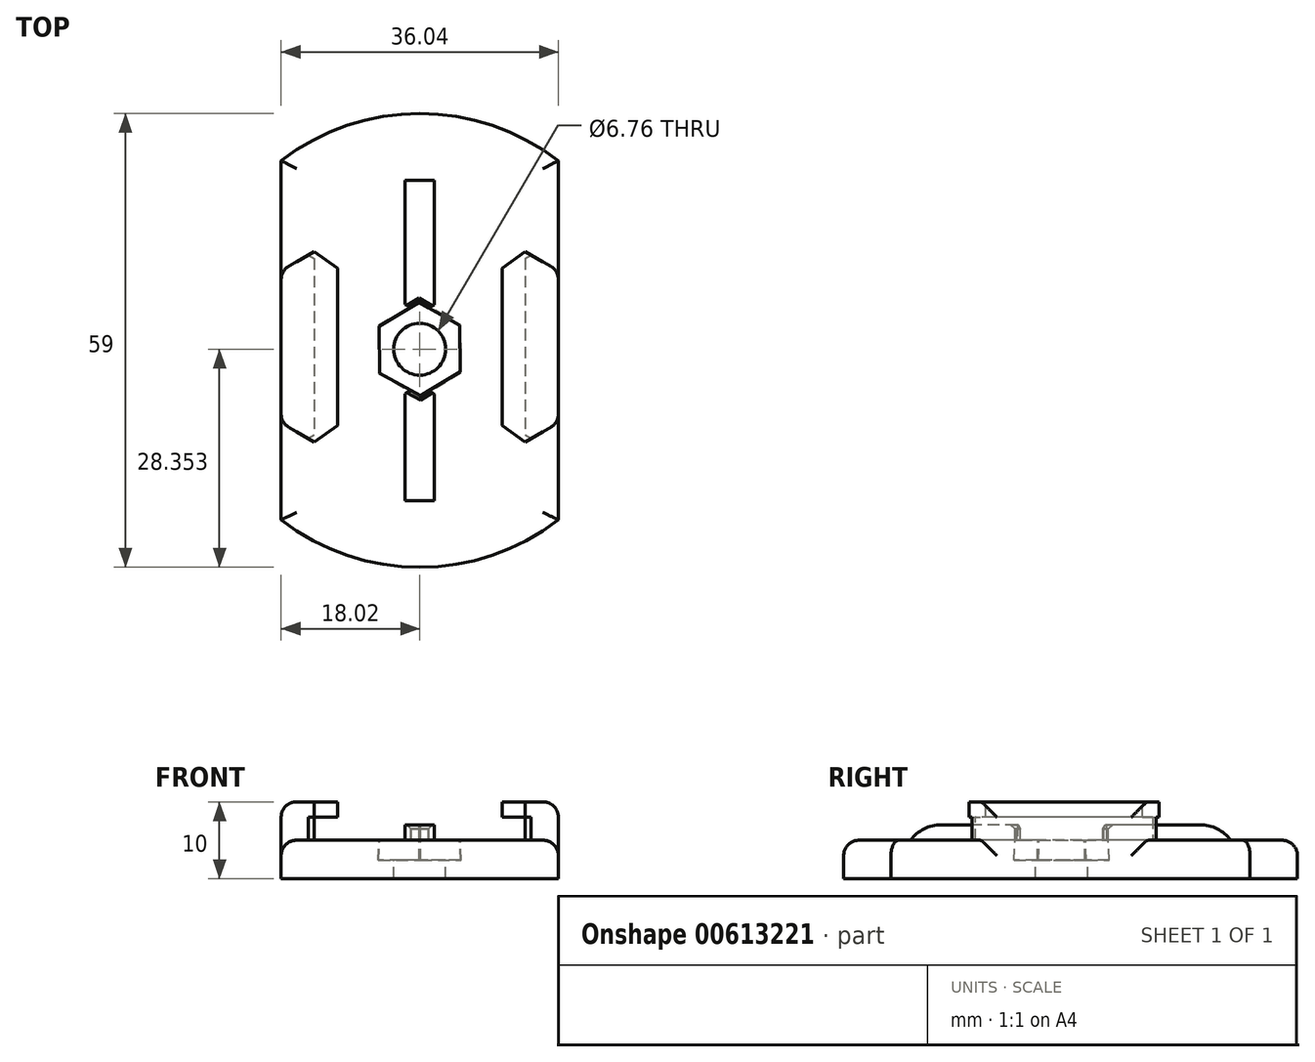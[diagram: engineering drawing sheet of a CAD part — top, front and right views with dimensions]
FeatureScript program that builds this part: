
annotation { "Feature Type Name" : "Feature", "Feature Type Description" : "" }
export const myFeature = defineFeature(function(context is Context, id is Id, definition is map)
    precondition{}
    {
        {
            var Q0;
            Q0=qCreatedBy(makeId("Top.planeOp"),FACE);
            var sketch = newSketch(context, id + "F0", { "sketchPlane" : qUnion([Q0])});
            skArc(sketch, "E0", {"start": v(-18.02, -23.35) * mm, "mid": v(0, -29.5) * mm, "end": v(18.02, -23.35) * mm});
            skLineSegment(sketch, "E1", {"start": v(-18.02, 23.35) * mm, "end": v(-18.02, -23.35) * mm});
            skLineSegment(sketch, "E2.MirrorCS", {"start": v(18.02, 23.35) * mm, "end": v(18.02, -23.35) * mm});
            skArc(sketch, "E3.trimOffspring", {"start": v(18.02, 23.35) * mm, "mid": v(0, 29.5) * mm, "end": v(-18.02, 23.35) * mm});
            skSolve(sketch);
        }
        {
            var Q0;
            Q0=qSketchRegion(id+"F0",true);
            extrude(context, id + "F1", {"entities" : qUnion([Q0]), "depth" : 5 * mm});
        }
        {
            var Q0;
            Q0=makeQuery(id+"F1.opExtrude","CAP_FACE",FACE,{"disambiguationData":[OSD([sQuery(id+"F0.wireOp",EDGE,"E0"),sQuery(id+"F0.wireOp",EDGE,"E1"),sQuery(id+"F0.wireOp",EDGE,"E2.MirrorCS"),sQuery(id+"F0.wireOp",EDGE,"E3.trimOffspring")])],"isStart":false});
            var sketch = newSketch(context, id + "F2", { "sketchPlane" : qUnion([Q0])});
            skPoint(sketch, "E4", {"position": v(-13.74, 11.54) * mm});
            skPoint(sketch, "E5", {"position": v(-13.74, -13.21) * mm});
            skLineSegment(sketch, "E6", {"start": v(-13.74, 11.54) * mm, "end": v(-18.02, 9.06) * mm});
            skLineSegment(sketch, "E7", {"start": v(-18.02, 9.06) * mm, "end": v(-18.02, -10.74) * mm});
            skLineSegment(sketch, "E8", {"start": v(-18.02, -10.74) * mm, "end": v(-13.74, -13.21) * mm});
            skLineSegment(sketch, "E9", {"start": v(-13.74, 11.54) * mm, "end": v(-13.74, -13.21) * mm});
            skLineSegment(sketch, "E10.MirrorCS", {"start": v(13.74, 11.54) * mm, "end": v(18.02, 9.06) * mm});
            skLineSegment(sketch, "E11.MirrorCS", {"start": v(13.74, 11.54) * mm, "end": v(13.74, -13.21) * mm});
            skLineSegment(sketch, "E12.MirrorCS", {"start": v(18.02, -10.74) * mm, "end": v(13.74, -13.21) * mm});
            skLineSegment(sketch, "E13.MirrorCS", {"start": v(18.02, 9.06) * mm, "end": v(18.02, -10.74) * mm});
            skSolve(sketch);
        }
        {
            var Q0;
            Q0=makeQuery(id+"F2.imprint","IMPRINT",FACE,{"disambiguationData":[TD([[makeQuery(id+"F2.imprint","IMPRINT",EDGE,{"derivedFrom":sQuery(id+"F2.wireOp",EDGE,"E6")}),1.0]])]});
            var Q1;
            Q1=makeQuery(id+"F2.imprint","IMPRINT",FACE,{"disambiguationData":[TD([[makeQuery(id+"F2.imprint","IMPRINT",EDGE,{"derivedFrom":sQuery(id+"F2.wireOp",EDGE,"E10.MirrorCS")}),-1.0]])]});
            extrude(context, id + "F3", {"entities" : qUnion([Q0, Q1]), "operationType" : NewBodyOperationType.ADD, "depth" : 5 * mm});
        }
        {
            var Q0;
            Q0=makeQuery(id+"F3.opExtrude","CAP_FACE",FACE,{"disambiguationData":[OSD([sQuery(id+"F2.wireOp",EDGE,"E6"),sQuery(id+"F2.wireOp",EDGE,"E7"),sQuery(id+"F2.wireOp",EDGE,"E8"),sQuery(id+"F2.wireOp",EDGE,"E9")])],"isStart":false});
            var sketch = newSketch(context, id + "F4", { "sketchPlane" : qUnion([Q0])});
            skPoint(sketch, "E14", {"position": v(-18.02, -0.84) * mm});
            skLineSegment(sketch, "E15", {"start": v(-10.7, 9.38) * mm, "end": v(-10.7, -11.05) * mm});
            skPoint(sketch, "E16", {"position": v(-10.7, -0.84) * mm});
            skLineSegment(sketch, "E17", {"start": v(-10.7, 9.38) * mm, "end": v(-13.74, 11.54) * mm});
            skLineSegment(sketch, "E18", {"start": v(-13.74, 11.54) * mm, "end": v(-13.74, -13.21) * mm});
            skLineSegment(sketch, "E19", {"start": v(-13.74, -13.21) * mm, "end": v(-10.7, -11.05) * mm});
            skLineSegment(sketch, "E20.MirrorCS", {"start": v(10.7, 9.38) * mm, "end": v(13.74, 11.54) * mm});
            skLineSegment(sketch, "E21.MirrorCS", {"start": v(10.7, 9.38) * mm, "end": v(10.7, -11.05) * mm});
            skLineSegment(sketch, "E22.MirrorCS", {"start": v(13.74, -13.21) * mm, "end": v(10.7, -11.05) * mm});
            skLineSegment(sketch, "E23.MirrorCS", {"start": v(13.74, 11.54) * mm, "end": v(13.74, -13.21) * mm});
            skSolve(sketch);
        }
        {
            var Q0;
            Q0=qSketchRegion(id+"F4",true);
            extrude(context, id + "F5", {"entities" : qUnion([Q0]), "operationType" : NewBodyOperationType.ADD, "oppositeDirection" : true, "depth" : 2 * mm});
        }
        {
            var Q0;
            Q0=makeQuery(id+"F1.opExtrude","CAP_FACE",FACE,{"disambiguationData":[OSD([sQuery(id+"F0.wireOp",EDGE,"E0"),sQuery(id+"F0.wireOp",EDGE,"E1"),sQuery(id+"F0.wireOp",EDGE,"E2.MirrorCS"),sQuery(id+"F0.wireOp",EDGE,"E3.trimOffspring")])],"isStart":false});
            var sketch = newSketch(context, id + "F6", { "sketchPlane" : qUnion([Q0])});
            skLineSegment(sketch, "E24.bottom", {"start": v(1.9, 20.83) * mm, "end": v(-1.9, 20.83) * mm});
            skLineSegment(sketch, "E24.top", {"start": v(1.9, -20.83) * mm, "end": v(-1.9, -20.83) * mm});
            skLineSegment(sketch, "E24.left", {"start": v(1.9, 20.83) * mm, "end": v(1.9, -20.83) * mm});
            skLineSegment(sketch, "E24.right", {"start": v(-1.9, 20.83) * mm, "end": v(-1.9, -20.83) * mm});
            skPoint(sketch, "E24.middle", {"position": v(0, 0) * mm});
            skSolve(sketch);
        }
        {
            var Q0;
            Q0=makeQuery(id+"F6.imprint","IMPRINT",FACE,{"disambiguationData":[TD([[makeQuery(id+"F6.imprint","IMPRINT",EDGE,{"derivedFrom":sQuery(id+"F6.wireOp",EDGE,"E24.bottom")}),1.0]])]});
            extrude(context, id + "F7", {"entities" : qUnion([Q0]), "operationType" : NewBodyOperationType.ADD, "depth" : 2 * mm});
        }
        {
            var Q0;
            Q0=makeQuery(id+"F7.opExtrude","CAP_EDGE",EDGE,{"disambiguationData":[OSD([sQuery(id+"F6.wireOp",EDGE,"E24.bottom")])],"isStart":false});
            var Q1;
            Q1=makeQuery(id+"F7.opExtrude","CAP_EDGE",EDGE,{"disambiguationData":[OSD([sQuery(id+"F6.wireOp",EDGE,"E24.top")])],"isStart":false});
            fillet(context, id + "F8", {"entities" : qUnion([Q0, Q1]), "radius" : 5 * mm, "tangentPropagation" : true, "allowEdgeOverflow" : false});
        }
        {
            var Q0;
            Q0=makeQuery(id+"F1.opExtrude","CAP_FACE",FACE,{"disambiguationData":[OSD([sQuery(id+"F0.wireOp",EDGE,"E0"),sQuery(id+"F0.wireOp",EDGE,"E1"),sQuery(id+"F0.wireOp",EDGE,"E2.MirrorCS"),sQuery(id+"F0.wireOp",EDGE,"E3.trimOffspring")])],"isStart":false});
            var sketch = newSketch(context, id + "F9", { "sketchPlane" : qUnion([Q0])});
            skCircle(sketch, "E25.cCircle", {"center": v(0, -1.15) * mm, "radius": 5.24 * mm, "construction": true});
            skLineSegment(sketch, "E25.0", {"start": v(-0.1, 4.9) * mm, "end": v(5.2, 1.96) * mm});
            skLineSegment(sketch, "E25.1", {"start": v(5.2, 1.96) * mm, "end": v(5.28, -4.1) * mm});
            skLineSegment(sketch, "E25.2", {"start": v(5.28, -4.1) * mm, "end": v(0.1, -7.2) * mm});
            skLineSegment(sketch, "E25.3", {"start": v(0.1, -7.2) * mm, "end": v(-5.2, -4.25) * mm});
            skLineSegment(sketch, "E25.4", {"start": v(-5.2, -4.25) * mm, "end": v(-5.28, 1.8) * mm});
            skLineSegment(sketch, "E25.5", {"start": v(-5.28, 1.8) * mm, "end": v(-0.1, 4.9) * mm});
            skPoint(sketch, "E25.0.midPoint", {"position": v(2.55, 3.43) * mm});
            skSolve(sketch);
        }
        {
            var Q0;
            Q0=qSketchRegion(id+"F9",true);
            extrude(context, id + "F10", {"entities" : qUnion([Q0]), "operationType" : NewBodyOperationType.REMOVE, "oppositeDirection" : true, "depth" : 2.6 * mm, "hasDraft" : true, "draftAngle" : 3 * degree, "hasSecondDirection" : true, "secondDirectionOppositeDirection" : false, "secondDirectionDepth" : 25 * mm});
        }
        {
            var Q0;
            Q0=sQuery(id+"F9.wireOp",VERTEX,"E25.cCircle.center");
            var Q1;
            Q1=makeQuery(id+"F1.opExtrude","SWEPT_BODY",BODY,{"disambiguationData":[OSD([sQuery(id+"F0.wireOp",EDGE,"E0"),sQuery(id+"F0.wireOp",EDGE,"E1"),sQuery(id+"F0.wireOp",EDGE,"E2.MirrorCS"),sQuery(id+"F0.wireOp",EDGE,"E3.trimOffspring")])]});
            hole(context, id + "F11", {"style" : HoleStyle.SIMPLE, "endStyle" : HoleEndStyle.THROUGH, "standardTappedOrClearance" : lookupTablePath({ "standard" : "ANSI", "fit" : "Normal (ASME)", "size" : "1/4", "type" : "Clearance" }), "standardBlindInLast" : lookupTablePath({ "fit" : "Free", "standard" : "ANSI", "size" : "1/4", "type" : "Clearance" }), "holeDiameter" : 6.76 * mm, "tappedDepth" : 12 * mm, "tapClearance" : 3, "locations" : qUnion([Q0]), "scope" : qUnion([Q1])});
        }
        {
            var Q0;
            Q0=makeQuery(id+"F5.boolean.opBoolean","SPLIT",EDGE,{"derivedFrom":makeQuery(id+"F3.opExtrude","SWEPT_EDGE",EDGE,{"disambiguationData":[OSD([sQuery(id+"F2.wireOp",EDGE,"E8"),sQuery(id+"F2.wireOp",EDGE,"E9")])]})});
            var Q1;
            Q1=makeQuery(id+"F5.boolean.opBoolean","SPLIT",EDGE,{"derivedFrom":makeQuery(id+"F3.opExtrude","SWEPT_EDGE",EDGE,{"disambiguationData":[OSD([sQuery(id+"F2.wireOp",EDGE,"E11.MirrorCS"),sQuery(id+"F2.wireOp",EDGE,"E12.MirrorCS")])]})});
            var Q2;
            Q2=makeQuery(id+"F5.boolean.opBoolean","SPLIT",EDGE,{"derivedFrom":makeQuery(id+"F3.opExtrude","SWEPT_EDGE",EDGE,{"disambiguationData":[OSD([sQuery(id+"F2.wireOp",EDGE,"E6"),sQuery(id+"F2.wireOp",EDGE,"E9")])]})});
            var Q3;
            Q3=makeQuery(id+"F5.boolean.opBoolean","SPLIT",EDGE,{"derivedFrom":makeQuery(id+"F3.opExtrude","SWEPT_EDGE",EDGE,{"disambiguationData":[OSD([sQuery(id+"F2.wireOp",EDGE,"E10.MirrorCS"),sQuery(id+"F2.wireOp",EDGE,"E11.MirrorCS")])]})});
            var Q4;
            Q4=makeQuery(id+"F10.boolean.opBoolean","INTERSECT",EDGE,{"derivedFrom":[makeQuery(id+"F7.opExtrude","SWEPT_FACE",FACE,{"disambiguationData":[OSD([sQuery(id+"F6.wireOp",EDGE,"E24.left")])]}),makeQuery(id+"F10.*.split.splitOp","SPLIT",FACE,{"derivedFrom":makeQuery(id+"F10.opExtrude","SWEPT_FACE",FACE,{"disambiguationData":[OSD([sQuery(id+"F9.wireOp",EDGE,"E25.0")])]}),"isFromBackBody":true})]});
            var Q5;
            Q5=makeQuery(id+"F10.boolean.opBoolean","INTERSECT",EDGE,{"derivedFrom":[makeQuery(id+"F7.opExtrude","SWEPT_FACE",FACE,{"disambiguationData":[OSD([sQuery(id+"F6.wireOp",EDGE,"E24.right")])]}),makeQuery(id+"F10.*.split.splitOp","SPLIT",FACE,{"derivedFrom":makeQuery(id+"F10.opExtrude","SWEPT_FACE",FACE,{"disambiguationData":[OSD([sQuery(id+"F9.wireOp",EDGE,"E25.5")])]}),"isFromBackBody":true})]});
            var Q6;
            Q6=makeQuery(id+"F10.boolean.opBoolean","INTERSECT",EDGE,{"derivedFrom":[makeQuery(id+"F7.opExtrude","CAP_FACE",FACE,{"disambiguationData":[OSD([sQuery(id+"F6.wireOp",EDGE,"E24.bottom"),sQuery(id+"F6.wireOp",EDGE,"E24.top"),sQuery(id+"F6.wireOp",EDGE,"E24.left"),sQuery(id+"F6.wireOp",EDGE,"E24.right")])],"isStart":false}),makeQuery(id+"F10.*.split.splitOp","SPLIT",FACE,{"derivedFrom":makeQuery(id+"F10.opExtrude","SWEPT_FACE",FACE,{"disambiguationData":[OSD([sQuery(id+"F9.wireOp",EDGE,"E25.5")])]}),"isFromBackBody":true})]});
            var Q7;
            Q7=makeQuery(id+"F10.boolean.opBoolean","INTERSECT",EDGE,{"derivedFrom":[makeQuery(id+"F7.opExtrude","CAP_FACE",FACE,{"disambiguationData":[OSD([sQuery(id+"F6.wireOp",EDGE,"E24.bottom"),sQuery(id+"F6.wireOp",EDGE,"E24.top"),sQuery(id+"F6.wireOp",EDGE,"E24.left"),sQuery(id+"F6.wireOp",EDGE,"E24.right")])],"isStart":false}),makeQuery(id+"F10.*.split.splitOp","SPLIT",FACE,{"derivedFrom":makeQuery(id+"F10.opExtrude","SWEPT_FACE",FACE,{"disambiguationData":[OSD([sQuery(id+"F9.wireOp",EDGE,"E25.0")])]}),"isFromBackBody":true})]});
            var Q8;
            Q8=makeQuery(id+"F10.boolean.opBoolean","INTERSECT",EDGE,{"derivedFrom":[makeQuery(id+"F7.opExtrude","CAP_FACE",FACE,{"disambiguationData":[OSD([sQuery(id+"F6.wireOp",EDGE,"E24.bottom"),sQuery(id+"F6.wireOp",EDGE,"E24.top"),sQuery(id+"F6.wireOp",EDGE,"E24.left"),sQuery(id+"F6.wireOp",EDGE,"E24.right")])],"isStart":false}),makeQuery(id+"F10.*.split.splitOp","SPLIT",FACE,{"derivedFrom":makeQuery(id+"F10.opExtrude","SWEPT_FACE",FACE,{"disambiguationData":[OSD([sQuery(id+"F9.wireOp",EDGE,"E25.3")])]}),"isFromBackBody":true})]});
            var Q9;
            Q9=makeQuery(id+"F10.boolean.opBoolean","INTERSECT",EDGE,{"derivedFrom":[makeQuery(id+"F7.opExtrude","CAP_FACE",FACE,{"disambiguationData":[OSD([sQuery(id+"F6.wireOp",EDGE,"E24.bottom"),sQuery(id+"F6.wireOp",EDGE,"E24.top"),sQuery(id+"F6.wireOp",EDGE,"E24.left"),sQuery(id+"F6.wireOp",EDGE,"E24.right")])],"isStart":false}),makeQuery(id+"F10.*.split.splitOp","SPLIT",FACE,{"derivedFrom":makeQuery(id+"F10.opExtrude","SWEPT_FACE",FACE,{"disambiguationData":[OSD([sQuery(id+"F9.wireOp",EDGE,"E25.2")])]}),"isFromBackBody":true})]});
            var Q10;
            Q10=makeQuery(id+"F10.boolean.opBoolean","INTERSECT",EDGE,{"derivedFrom":[makeQuery(id+"F7.opExtrude","SWEPT_FACE",FACE,{"disambiguationData":[OSD([sQuery(id+"F6.wireOp",EDGE,"E24.left")])]}),makeQuery(id+"F10.*.split.splitOp","SPLIT",FACE,{"derivedFrom":makeQuery(id+"F10.opExtrude","SWEPT_FACE",FACE,{"disambiguationData":[OSD([sQuery(id+"F9.wireOp",EDGE,"E25.2")])]}),"isFromBackBody":true})]});
            var Q11;
            Q11=makeQuery(id+"F10.boolean.opBoolean","INTERSECT",EDGE,{"derivedFrom":[makeQuery(id+"F7.opExtrude","SWEPT_FACE",FACE,{"disambiguationData":[OSD([sQuery(id+"F6.wireOp",EDGE,"E24.right")])]}),makeQuery(id+"F10.*.split.splitOp","SPLIT",FACE,{"derivedFrom":makeQuery(id+"F10.opExtrude","SWEPT_FACE",FACE,{"disambiguationData":[OSD([sQuery(id+"F9.wireOp",EDGE,"E25.3")])]}),"isFromBackBody":true})]});
            chamfer(context, id + "F12", {"entities" : qUnion([Q0, Q1, Q2, Q3, Q4, Q5, Q6, Q7, Q8, Q9, Q10, Q11]), "width" : .5 * mm});
        }
        {
            var Q0;
            Q0=makeQuery(id+"F3.opExtrude","CAP_EDGE",EDGE,{"disambiguationData":[OSD([sQuery(id+"F2.wireOp",EDGE,"E7")])],"isStart":false});
            var Q1;
            Q1=makeQuery(id+"F3.opExtrude","CAP_EDGE",EDGE,{"disambiguationData":[OSD([sQuery(id+"F2.wireOp",EDGE,"E13.MirrorCS")])],"isStart":false});
            var Q2;
            Q2=makeQuery(id+"F3.opExtrude","SWEPT_EDGE",EDGE,{"disambiguationData":[OSD([sQuery(id+"F0.wireOp",EDGE,"E2.MirrorCS"),sQuery(id+"F2.wireOp",EDGE,"E12.MirrorCS"),sQuery(id+"F2.wireOp",EDGE,"E13.MirrorCS")])]});
            var Q3;
            Q3=makeQuery(id+"F3.opExtrude","SWEPT_EDGE",EDGE,{"disambiguationData":[OSD([sQuery(id+"F0.wireOp",EDGE,"E1"),sQuery(id+"F2.wireOp",EDGE,"E7"),sQuery(id+"F2.wireOp",EDGE,"E8")])]});
            var Q4;
            Q4=makeQuery(id+"F3.opExtrude","SWEPT_EDGE",EDGE,{"disambiguationData":[OSD([sQuery(id+"F0.wireOp",EDGE,"E1"),sQuery(id+"F2.wireOp",EDGE,"E6"),sQuery(id+"F2.wireOp",EDGE,"E7")])]});
            var Q5;
            Q5=makeQuery(id+"F3.opExtrude","SWEPT_EDGE",EDGE,{"disambiguationData":[OSD([sQuery(id+"F0.wireOp",EDGE,"E2.MirrorCS"),sQuery(id+"F2.wireOp",EDGE,"E10.MirrorCS"),sQuery(id+"F2.wireOp",EDGE,"E13.MirrorCS")])]});
            var Q6;
            {var subQ0=sQuery(id+"F0.wireOp",EDGE,"E3.trimOffspring");var subQ1=sQuery(id+"F0.wireOp",EDGE,"E2.MirrorCS");Q6=makeQuery(id+"F3.boolean.opBoolean","SPLIT",EDGE,{"disambiguationData":[TD([makeQuery(id+"F1.opExtrude","SWEPT_FACE",FACE,{"disambiguationData":[OSD([subQ0])]})])],"derivedFrom":makeQuery(id+"F1.opExtrude","CAP_EDGE",EDGE,{"disambiguationData":[OSD([subQ1])],"isStart":false})});}
            var Q7;
            Q7=makeQuery(id+"F1.opExtrude","CAP_EDGE",EDGE,{"disambiguationData":[OSD([sQuery(id+"F0.wireOp",EDGE,"E3.trimOffspring")])],"isStart":false});
            var Q8;
            {var subQ0=sQuery(id+"F0.wireOp",EDGE,"E3.trimOffspring");var subQ1=sQuery(id+"F0.wireOp",EDGE,"E1");Q8=makeQuery(id+"F3.boolean.opBoolean","SPLIT",EDGE,{"disambiguationData":[TD([makeQuery(id+"F1.opExtrude","SWEPT_FACE",FACE,{"disambiguationData":[OSD([subQ0])]})])],"derivedFrom":makeQuery(id+"F1.opExtrude","CAP_EDGE",EDGE,{"disambiguationData":[OSD([subQ1])],"isStart":false})});}
            var Q9;
            {var subQ0=sQuery(id+"F0.wireOp",EDGE,"E0");var subQ1=sQuery(id+"F0.wireOp",EDGE,"E2.MirrorCS");Q9=makeQuery(id+"F3.boolean.opBoolean","SPLIT",EDGE,{"disambiguationData":[TD([makeQuery(id+"F1.opExtrude","SWEPT_FACE",FACE,{"disambiguationData":[OSD([subQ0])]})])],"derivedFrom":makeQuery(id+"F1.opExtrude","CAP_EDGE",EDGE,{"disambiguationData":[OSD([subQ1])],"isStart":false})});}
            var Q10;
            Q10=makeQuery(id+"F1.opExtrude","CAP_EDGE",EDGE,{"disambiguationData":[OSD([sQuery(id+"F0.wireOp",EDGE,"E0")])],"isStart":false});
            var Q11;
            {var subQ0=sQuery(id+"F0.wireOp",EDGE,"E1");var subQ1=sQuery(id+"F0.wireOp",EDGE,"E0");Q11=makeQuery(id+"F3.boolean.opBoolean","SPLIT",EDGE,{"disambiguationData":[TD([makeQuery(id+"F1.opExtrude","SWEPT_FACE",FACE,{"disambiguationData":[OSD([subQ1])]})])],"derivedFrom":makeQuery(id+"F1.opExtrude","CAP_EDGE",EDGE,{"disambiguationData":[OSD([subQ0])],"isStart":false})});}
            fillet(context, id + "F13", {"entities" : qUnion([Q0, Q1, Q2, Q3, Q4, Q5, Q6, Q7, Q8, Q9, Q10, Q11]), "radius" : 2 * mm, "tangentPropagation" : true, "allowEdgeOverflow" : false});
        }
    });
